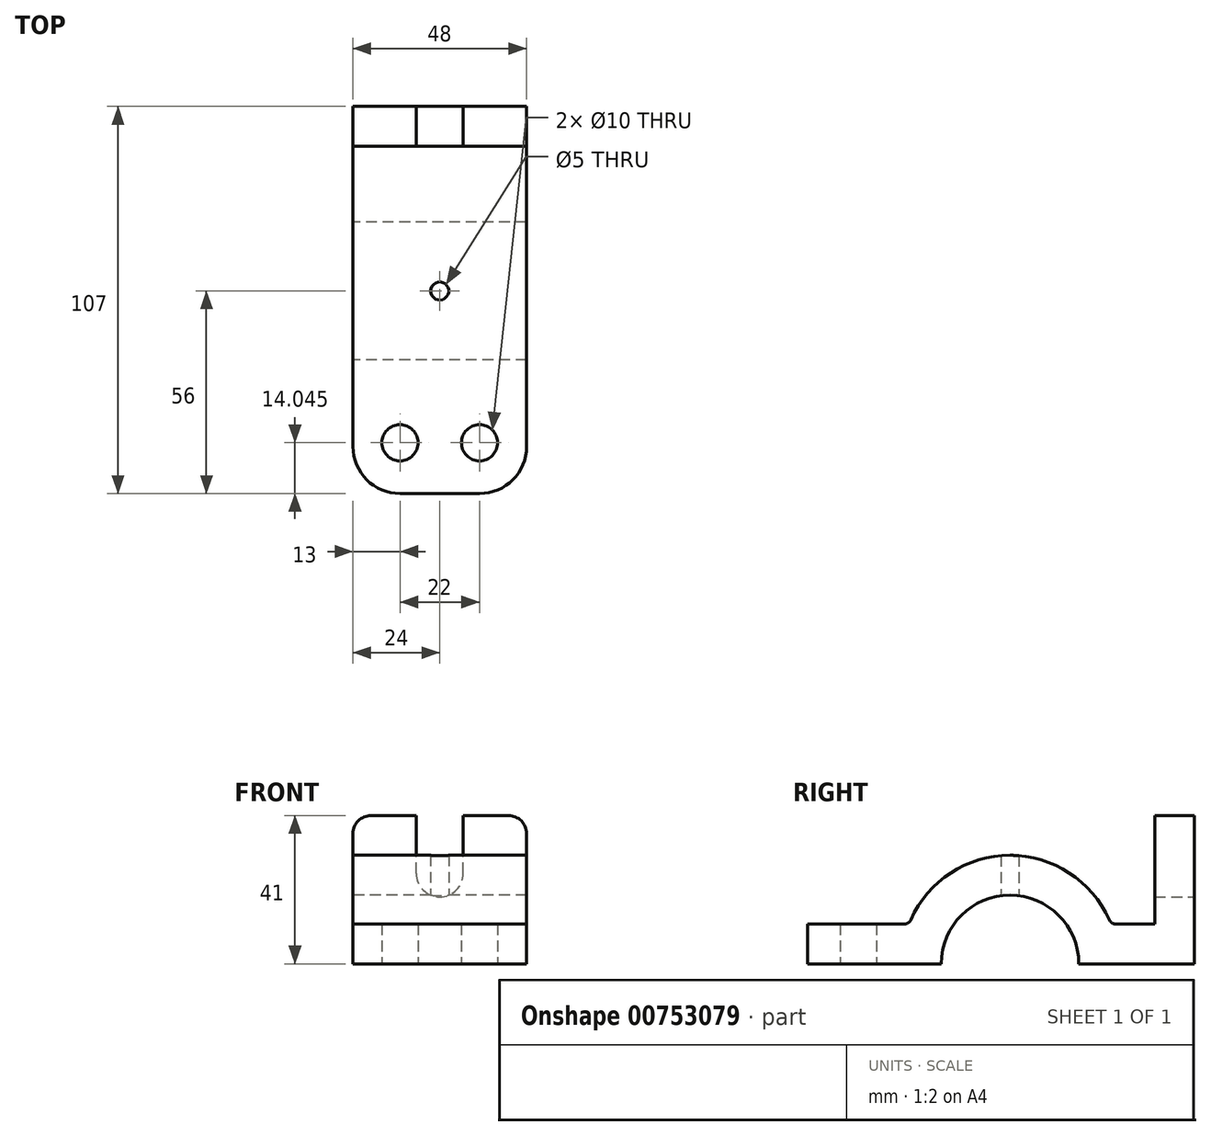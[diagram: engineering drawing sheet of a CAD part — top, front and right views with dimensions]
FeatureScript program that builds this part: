
annotation { "Feature Type Name" : "Feature", "Feature Type Description" : "" }
export const myFeature = defineFeature(function(context is Context, id is Id, definition is map)
    precondition{}
    {
        {
            var Q0;
            Q0=qCreatedBy(makeId("Right.planeOp"),FACE);
            var sketch = newSketch(context, id + "F0", { "sketchPlane" : qUnion([Q0])});
            skCircle(sketch, "E0", {"center": v(0, 0) * mm, "radius": 19 * mm});
            skCircle(sketch, "E1", {"center": v(0, 0) * mm, "radius": 30 * mm});
            skLineSegment(sketch, "E2.bottom", {"start": v(-56, 11) * mm, "end": v(51, 11) * mm});
            skLineSegment(sketch, "E2.top", {"start": v(-56, 0) * mm, "end": v(51, 0) * mm});
            skLineSegment(sketch, "E2.left", {"start": v(-56, 11) * mm, "end": v(-56, 0) * mm});
            skLineSegment(sketch, "E2.right", {"start": v(51, 11) * mm, "end": v(51, 0) * mm});
            skLineSegment(sketch, "E3.bottom", {"start": v(51, 11) * mm, "end": v(40, 11) * mm});
            skLineSegment(sketch, "E3.top", {"start": v(51, 41) * mm, "end": v(40, 41) * mm});
            skLineSegment(sketch, "E3.left", {"start": v(51, 11) * mm, "end": v(51, 41) * mm});
            skLineSegment(sketch, "E3.right", {"start": v(40, 11) * mm, "end": v(40, 41) * mm});
            skSolve(sketch);
        }
        {
            var Q0;
            {var subQ5=sQuery(id+"F0.wireOp",EDGE,"E2.left");Q0=makeQuery(id+"F0.imprint","IMPRINT",FACE,{"disambiguationData":[TD([[makeQuery(id+"F0.imprint","IMPRINT",EDGE,{"derivedFrom":subQ5}),1.0]])]});}
            var Q1;
            Q1=makeQuery(id+"F0.imprint","IMPRINT",FACE,{"disambiguationData":[TD([[makeQuery(id+"F0.imprint","IMPRINT",EDGE,{"derivedFrom":sQuery(id+"F0.wireOp",EDGE,"E3.top")}),1.0]])]});
            var Q2;
            {var subQ0=sQuery(id+"F0.wireOp",EDGE,"E2.right");Q2=makeQuery(id+"F0.imprint","IMPRINT",FACE,{"disambiguationData":[TD([[makeQuery(id+"F0.imprint","IMPRINT",EDGE,{"derivedFrom":subQ0}),-1.0]])]});}
            var Q3;
            {var subQ0=sQuery(id+"F0.wireOp",EDGE,"E2.bottom");var subQ1=sQuery(id+"F0.wireOp",EDGE,"E0");var subQ2=makeQuery(id+"F0.imprint","INTERSECT",VERTEX,{"disambiguationData":[OD(0.0)],"derivedFrom":[subQ1,subQ0]});Q3=makeQuery(id+"F0.imprint","IMPRINT",FACE,{"disambiguationData":[TD([[makeQuery(id+"F0.imprint","IMPRINT",EDGE,{"disambiguationData":[TD([[subQ2,1.0]])],"derivedFrom":subQ1}),-1.0]])]});}
            var Q4;
            {var subQ0=sQuery(id+"F0.wireOp",EDGE,"E2.bottom");var subQ1=sQuery(id+"F0.wireOp",EDGE,"E0");var subQ2=makeQuery(id+"F0.imprint","INTERSECT",VERTEX,{"disambiguationData":[OD(1.0)],"derivedFrom":[subQ1,subQ0]});Q4=makeQuery(id+"F0.imprint","IMPRINT",FACE,{"disambiguationData":[TD([[makeQuery(id+"F0.imprint","IMPRINT",EDGE,{"disambiguationData":[TD([[subQ2,1.0]])],"derivedFrom":subQ1}),-1.0]])]});}
            var Q5;
            {var subQ0=sQuery(id+"F0.wireOp",EDGE,"E2.bottom");var subQ1=sQuery(id+"F0.wireOp",EDGE,"E0");var subQ2=makeQuery(id+"F0.imprint","INTERSECT",VERTEX,{"disambiguationData":[OD(0.0)],"derivedFrom":[subQ1,subQ0]});Q5=makeQuery(id+"F0.imprint","IMPRINT",FACE,{"disambiguationData":[TD([[makeQuery(id+"F0.imprint","IMPRINT",EDGE,{"disambiguationData":[TD([[subQ2,-1.0]])],"derivedFrom":subQ1}),-1.0]])]});}
            extrude(context, id + "F1", {"entities" : qUnion([Q0, Q1, Q2, Q3, Q4, Q5]), "endBound" : BoundingType.SYMMETRIC, "depth" : 48 * mm, "offsetDistance" : 25 * mm});
        }
        {
            var Q0;
            Q0=makeQuery(id+"F1.opExtrude","SWEPT_FACE",FACE,{"disambiguationData":[OSD([sQuery(id+"F0.wireOp",EDGE,"E2.right"),sQuery(id+"F0.wireOp",EDGE,"E3.left")])]});
            var sketch = newSketch(context, id + "F2", { "sketchPlane" : qUnion([Q0])});
            skLineSegment(sketch, "E4", {"start": v(0, 0) * mm, "end": v(0, 41) * mm, "construction": true});
            skCircle(sketch, "E5", {"center": v(0, 25) * mm, "radius": 6.5 * mm});
            skLineSegment(sketch, "E6", {"start": v(-6.5, 25) * mm, "end": v(-6.5, 41) * mm});
            skLineSegment(sketch, "E7", {"start": v(6.5, 25) * mm, "end": v(6.5, 41) * mm});
            skSolve(sketch);
        }
        {
            var Q0;
            {var subQ0=sQuery(id+"F2.wireOp",EDGE,"E6");Q0=makeQuery(id+"F2.imprint","IMPRINT",FACE,{"disambiguationData":[TD([[makeQuery(id+"F2.imprint","IMPRINT",EDGE,{"derivedFrom":subQ0}),-1.0]])]});}
            var Q1;
            {var subQ0=sQuery(id+"F2.wireOp",EDGE,"E5");var subQ1=makeQuery(id+"F2.imprint","INTERSECT",VERTEX,{"derivedFrom":[subQ0,sQuery(id+"F2.wireOp",EDGE,"E6")]});Q1=makeQuery(id+"F2.imprint","IMPRINT",FACE,{"disambiguationData":[TD([[makeQuery(id+"F2.imprint","IMPRINT",EDGE,{"disambiguationData":[TD([[subQ1,1.0]])],"derivedFrom":subQ0}),1.0]])]});}
            var Q2;
            Q2=makeQuery(id+"F1.opExtrude","SWEPT_FACE",FACE,{"disambiguationData":[OSD([sQuery(id+"F0.wireOp",EDGE,"E3.right")])]});
            extrude(context, id + "F3", {"entities" : qUnion([Q0, Q1]), "operationType" : NewBodyOperationType.REMOVE, "endBound" : BoundingType.UP_TO_SURFACE, "oppositeDirection" : true, "depth" : 25 * mm, "endBoundEntityFace" : qUnion([Q2]), "offsetDistance" : 25 * mm});
        }
        {
            var Q0;
            Q0=qCreatedBy(makeId("Top.planeOp"),FACE);
            var sketch = newSketch(context, id + "F4", { "sketchPlane" : qUnion([Q0])});
            skCircle(sketch, "E8", {"center": v(0, 0) * mm, "radius": 2.5 * mm});
            skLineSegment(sketch, "E9", {"start": v(24, -41.96) * mm, "end": v(-24, -41.96) * mm, "construction": true});
            skLineSegment(sketch, "E10", {"start": v(0, -56) * mm, "end": v(0, -27.91) * mm, "construction": true});
            skCircle(sketch, "E11", {"center": v(-11, -41.96) * mm, "radius": 5 * mm});
            skCircle(sketch, "E12", {"center": v(11, -41.96) * mm, "radius": 5 * mm});
            skSolve(sketch);
        }
        {
            var Q0;
            Q0=makeQuery(id+"F4.imprint","IMPRINT",FACE,{"disambiguationData":[TD([[makeQuery(id+"F4.imprint","IMPRINT",EDGE,{"derivedFrom":sQuery(id+"F4.wireOp",EDGE,"E12")}),1.0]])]});
            var Q1;
            Q1=makeQuery(id+"F4.imprint","IMPRINT",FACE,{"disambiguationData":[TD([[makeQuery(id+"F4.imprint","IMPRINT",EDGE,{"derivedFrom":sQuery(id+"F4.wireOp",EDGE,"E11")}),1.0]])]});
            var Q2;
            Q2=makeQuery(id+"F4.imprint","IMPRINT",FACE,{"disambiguationData":[TD([[makeQuery(id+"F4.imprint","IMPRINT",EDGE,{"derivedFrom":sQuery(id+"F4.wireOp",EDGE,"E8")}),1.0]])]});
            extrude(context, id + "F5", {"entities" : qUnion([Q0, Q1, Q2]), "operationType" : NewBodyOperationType.REMOVE, "endBound" : BoundingType.THROUGH_ALL, "depth" : 25 * mm, "offsetDistance" : 25 * mm});
        }
        {
            var Q0;
            Q0=makeQuery(id+"F1.opExtrude","CAP_EDGE",EDGE,{"disambiguationData":[OSD([sQuery(id+"F0.wireOp",EDGE,"E2.left")])],"isStart":true});
            var Q1;
            Q1=makeQuery(id+"F1.opExtrude","CAP_EDGE",EDGE,{"disambiguationData":[OSD([sQuery(id+"F0.wireOp",EDGE,"E2.left")])],"isStart":false});
            fillet(context, id + "F6", {"entities" : qUnion([Q0, Q1]), "radius" : 13 * mm, "tangentPropagation" : true, "allowEdgeOverflow" : false});
        }
        {
            var Q0;
            Q0=makeQuery(id+"F1.opExtrude","CAP_EDGE",EDGE,{"disambiguationData":[OSD([sQuery(id+"F0.wireOp",EDGE,"E3.top")])],"isStart":true});
            var Q1;
            Q1=makeQuery(id+"F1.opExtrude","CAP_EDGE",EDGE,{"disambiguationData":[OSD([sQuery(id+"F0.wireOp",EDGE,"E3.top")])],"isStart":false});
            fillet(context, id + "F7", {"entities" : qUnion([Q0, Q1]), "radius" : 5 * mm, "tangentPropagation" : true, "allowEdgeOverflow" : false});
        }
        {
            var Q0;
            {var subQ0=sQuery(id+"F0.wireOp",EDGE,"E2.bottom");var subQ1=sQuery(id+"F0.wireOp",EDGE,"E1");Q0=makeQuery(id+"F1.opExtrude","SWEPT_EDGE",EDGE,{"disambiguationData":[OSD([subQ1,subQ0]),TDD([makeQuery(id+"F0.imprint","INTERSECT",VERTEX,{"disambiguationData":[OD(1.0)],"derivedFrom":[subQ1,subQ0]})])]});}
            var Q1;
            {var subQ0=sQuery(id+"F0.wireOp",EDGE,"E2.bottom");var subQ1=sQuery(id+"F0.wireOp",EDGE,"E1");Q1=makeQuery(id+"F1.opExtrude","SWEPT_EDGE",EDGE,{"disambiguationData":[OSD([subQ1,subQ0]),TDD([makeQuery(id+"F0.imprint","INTERSECT",VERTEX,{"disambiguationData":[OD(0.0)],"derivedFrom":[subQ1,subQ0]})])]});}
            fillet(context, id + "F8", {"entities" : qUnion([Q0, Q1]), "radius" : 2 * mm, "tangentPropagation" : true, "allowEdgeOverflow" : false});
        }
    });
